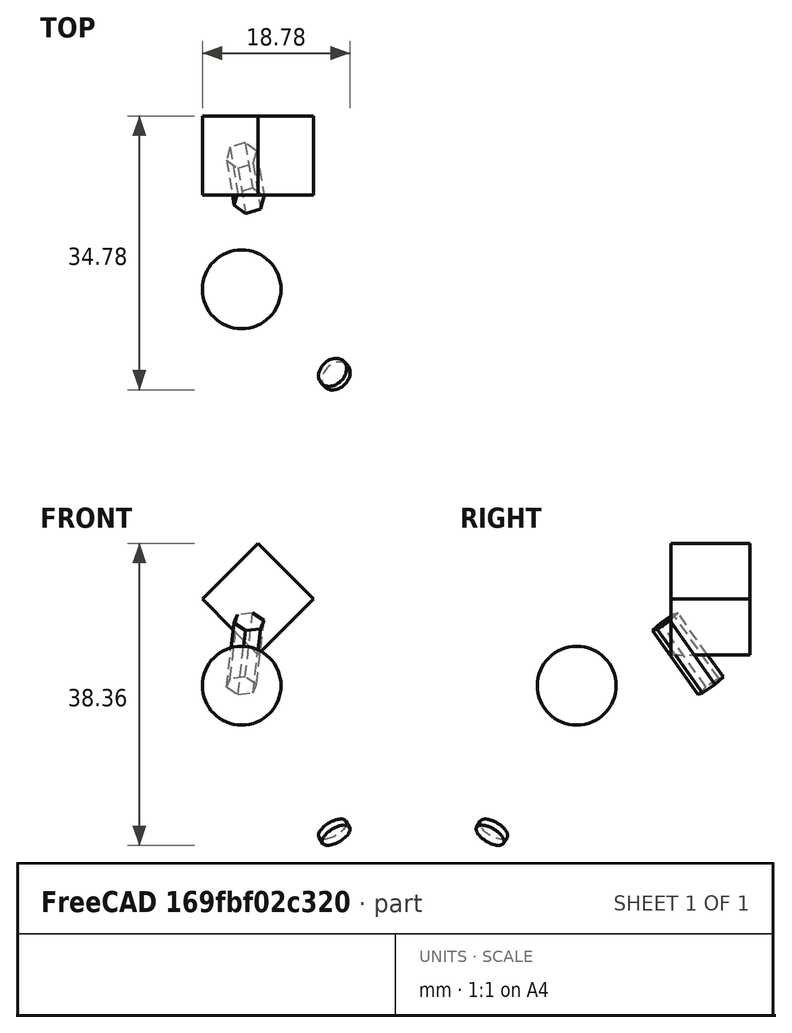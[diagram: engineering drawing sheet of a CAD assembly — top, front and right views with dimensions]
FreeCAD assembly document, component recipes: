
FREECAD ASSEMBLY — COMPONENT RECIPES ("nested-structure")

This assembly document has 4 components, labeled P0..P3 below (a component is one placed body or linked part). 2 of them carry a construction recipe — the FreeCAD feature program that regenerates the part from scratch, quoted from this document or its linked companion documents; the rest are supplied as boundary geometry only. No exploded tour is included for this assembly.
COMPONENT P0 — geometry summary ("external-file-mirror"; no construction recipe available for this part):
  bounding box: 4.0 x 3.5 x 3.5 mm
  tessellated surface: 500 triangles
  volume: 13 mm^3 (25% of its bounding box)
  symmetry: 2-fold rotationally symmetric about the y axis; mirror-symmetric across its y mid-plane
COMPONENT P1 — recipe-attached ("Link002", a linked part whose construction recipe lives in a companion FreeCAD document of the same project; that document's serialized recipe follows).
Construction recipe (the companion document, serialized — sketch geometry with constraints, then the solid features built on it; lengths are millimeters unless a unit is written):

FCSTD DOCUMENT  (FreeCAD 1.1R44874 (Git))
Label: external-file2
License: All rights reserved
LicenseURL: https://en.wikipedia.org/wiki/All_rights_reserved
objects: Part::Sphere×2, Part::Cylinder×1, Part::MultiCommon×1, App::Point×1, App::LinkGroupPython×1, App::Part×1
note: 4 computed .brp shape members not serialized (recipe doc carries the construction recipe); baked Part::Feature solids carry a one-line shape summary decoded from their .brp

FEATURE [Part::Sphere] Sphere
  Angle1 = -90
  Angle2 = 90
  Angle3 = 360
  AttacherType = Attacher::AttachEngine3D
  Placement = pos=(0,0,-2) rot=(0,0,1;0rad)
  Radius = 5
FEATURE [Part::Sphere] Sphere001
  Angle1 = -90
  Angle2 = 90
  Angle3 = 360
  AttacherType = Attacher::AttachEngine3D
  Placement = pos=(0,0,7) rot=(0,0,1;0rad)
  Radius = 5
FEATURE [Part::Cylinder] Cylinder
  Angle = 360
  AttacherType = Attacher::AttachEngine3D
  FirstAngle = 0
  Height = 10
  Placement = pos=(0,0,-3) rot=(0,0,1;0rad)
  Radius = 2
  SecondAngle = 0
FEATURE [Part::MultiCommon] Common
  Behavior = 0
  Refine = true
  Shapes = -> [Sphere,Sphere001,Cylinder]
FEATURE [App::Point] Origin001
  Role = Origin
FEATURE [App::LinkGroupPython] OpticalLensGroup  # WARN: FeaturePython — macro-defined, semantics opaque (R4)
  AbsorptionLength = inf
  ElementList = -> [Common]
  GratingDiffractionOrder = 1
  GratingLinesOrientation = (0,0,1)
  GratingLinesPerMillimeter = 1000
  GratingType = 0
  LinkMode = 0
  ModifyPhiDomain = 0, 2*pi
  ModifyThetaDomain = -pi/2, pi/2
  OpticalType = 1
  Placement = pos=(0,0,-2.5) rot=(0,0,1;0rad)
  PowerPhiDomain = 0, 2*pi
  PowerThetaDomain = -pi/2, pi/2
  RecordHits = false
  Reflectivity = 1
  RefractiveIndex = 1.4
FEATURE [App::Part] Part  label="spherical-lens"
  Group = -> [OpticalLensGroup]
  Origin = -> Origin
COMPONENT P2 — recipe-attached ("Part001", modeled in this document).
Construction recipe (the document's own serialized feature program — sketch geometry with constraints, then the solid features built on it; lengths are millimeters unless a unit is written):

FEATURE [PartDesign::AdditivePrism] Prism001
  AttacherType = Attacher::AttachEngine3D
  Circumradius = 2
  FirstAngle = 0
  Height = 10
  Polygon = 6
  Refine = true
  SecondAngle = 0
  Suppressed = false
FEATURE [PartDesign::Body] Body
  AllowCompound = false
  Group = -> [Prism001]
  Origin = -> Origin002
  Placement = pos=(0,0,0) rot=(2,0,1;0.698132rad)
  Tip = -> Prism001
COMPONENT P3 — geometry summary ("Part002"; no construction recipe available for this part):
  bounding box: 10.7 x 6.2 x 5.5 mm
  tessellated surface: 60 triangles
  volume: 312 mm^3 (85% of its bounding box)
PROVENANCE & LICENSES
A FreeCAD (.FCStd) document from a public repository crawl; recipes are the document's own serialized feature recipes (and, for linked parts, companion documents' recipes).
License: lgpl-3.0.
